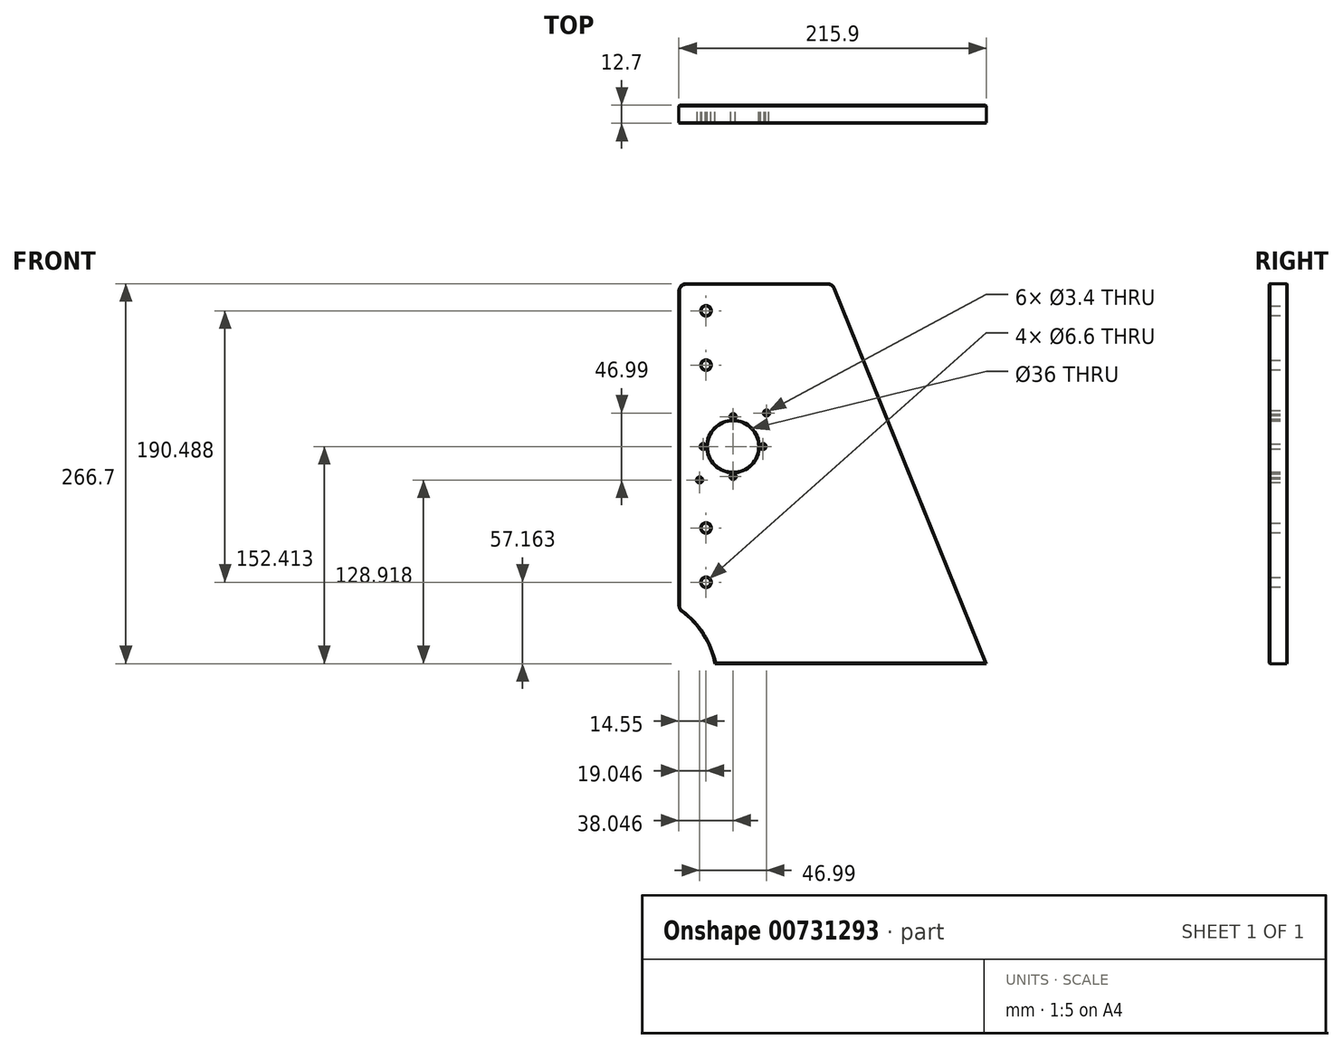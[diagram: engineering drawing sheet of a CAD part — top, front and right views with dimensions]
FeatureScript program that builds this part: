
annotation { "Feature Type Name" : "Feature", "Feature Type Description" : "" }
export const myFeature = defineFeature(function(context is Context, id is Id, definition is map)
    precondition{}
    {
        {
            var Q0;
            Q0=qCreatedBy(makeId("Front.planeOp"),FACE);
            var sketch = newSketch(context, id + "F0", { "sketchPlane" : qUnion([Q0])});
            skLineSegment(sketch, "E0.bottom", {"start": v(108.43, 152.4) * mm, "end": v(-107.47, 152.4) * mm});
            skLineSegment(sketch, "E0.left", {"start": v(108.43, 152.4) * mm, "end": v(108.43, -114.3) * mm});
            skLineSegment(sketch, "E0.right", {"start": v(-107.47, 152.4) * mm, "end": v(-107.47, -114.3) * mm});
            skPoint(sketch, "E0.middle", {"position": v(0, 0) * mm});
            skCircle(sketch, "E1", {"center": v(-88.42, -57.14) * mm, "radius": 3.3 * mm});
            skCircle(sketch, "E2", {"center": v(-88.42, -19.04) * mm, "radius": 3.3 * mm});
            skCircle(sketch, "E3", {"center": v(-88.42, 95.25) * mm, "radius": 3.3 * mm});
            skCircle(sketch, "E4", {"center": v(-88.42, 133.35) * mm, "radius": 3.3 * mm});
            skLineSegment(sketch, "E5", {"start": v(-107.47, -114.3) * mm, "end": v(108.43, -114.3) * mm});
            skLineSegment(sketch, "E6", {"start": v(-107.47, -76.2) * mm, "end": v(108.43, -76.2) * mm, "construction": true});
            skPoint(sketch, "E7.middle", {"position": v(-69.42, 38.11) * mm});
            skLineSegment(sketch, "E8", {"start": v(-69.42, 74.31) * mm, "end": v(-69.42, 11.11) * mm, "construction": true});
            skPoint(sketch, "E9.startSnap0", {"position": v(0.48, 152.4) * mm});
            skCircle(sketch, "E10", {"center": v(-69.42, 38.11) * mm, "radius": 18 * mm});
            skLineSegment(sketch, "E11", {"start": v(-98.77, 38.11) * mm, "end": v(-40.23, 38.11) * mm, "construction": true});
            skLineSegment(sketch, "E12", {"start": v(-91.1, 59.79) * mm, "end": v(-42.84, 11.53) * mm, "construction": true});
            skLineSegment(sketch, "E13", {"start": v(-49.22, 58.32) * mm, "end": v(-94.15, 13.39) * mm, "construction": true});
            skCircle(sketch, "E14", {"center": v(-92.92, 61.6) * mm, "radius": 1.7 * mm});
            skCircle(sketch, "E15.MirrorC", {"center": v(-92.92, 14.62) * mm, "radius": 1.7 * mm});
            skCircle(sketch, "E16.MirrorC", {"center": v(-45.93, 61.6) * mm, "radius": 1.7 * mm});
            skCircle(sketch, "E17.MirrorC", {"center": v(-45.93, 14.62) * mm, "radius": 1.7 * mm});
            skCircle(sketch, "E18", {"center": v(-69.42, 59.11) * mm, "radius": 1.7 * mm});
            skCircle(sketch, "E19.MirrorC", {"center": v(-69.42, 17.11) * mm, "radius": 1.7 * mm});
            skCircle(sketch, "E20", {"center": v(-90.42, 38.11) * mm, "radius": 1.7 * mm});
            skCircle(sketch, "E21.MirrorC", {"center": v(-48.42, 38.11) * mm, "radius": 1.7 * mm});
            skLineSegment(sketch, "E22", {"start": v(0.48, 152.4) * mm, "end": v(108.43, -114.3) * mm});
            skArc(sketch, "E23", {"start": v(-82.07, -114.3) * mm, "mid": v(-91, -92.73) * mm, "end": v(-107.47, -76.2) * mm});
            skSolve(sketch);
        }
        {
            var Q0;
            Q0=makeQuery(id+"F0.imprint","IMPRINT",FACE,{"disambiguationData":[TD([[makeQuery(id+"F0.imprint","IMPRINT",EDGE,{"derivedFrom":sQuery(id+"F0.wireOp",EDGE,"E1")}),-1.0]])]});
            var Q1;
            Q1=makeQuery(id+"F0.imprint","IMPRINT",FACE,{"disambiguationData":[TD([[makeQuery(id+"F0.imprint","IMPRINT",EDGE,{"derivedFrom":sQuery(id+"F0.wireOp",EDGE,"E15.MirrorC")}),-1.0]])]});
            var Q2;
            Q2=makeQuery(id+"F0.imprint","IMPRINT",FACE,{"disambiguationData":[TD([[makeQuery(id+"F0.imprint","IMPRINT",EDGE,{"derivedFrom":sQuery(id+"F0.wireOp",EDGE,"E17.MirrorC")}),1.0]])]});
            var Q3;
            Q3=makeQuery(id+"F0.imprint","IMPRINT",FACE,{"disambiguationData":[TD([[makeQuery(id+"F0.imprint","IMPRINT",EDGE,{"derivedFrom":sQuery(id+"F0.wireOp",EDGE,"E16.MirrorC")}),-1.0]])]});
            var Q4;
            Q4=makeQuery(id+"F0.imprint","IMPRINT",FACE,{"disambiguationData":[TD([[makeQuery(id+"F0.imprint","IMPRINT",EDGE,{"derivedFrom":sQuery(id+"F0.wireOp",EDGE,"E14")}),1.0]])]});
            extrude(context, id + "F1", {"entities" : qUnion([Q0, Q1, Q2, Q3, Q4]), "depth" : 12.7 * mm, "offsetDistance" : 25.4 * mm});
        }
        {
            var Q0;
            Q0=makeQuery(id+"F1.opExtrude","SWEPT_EDGE",EDGE,{"disambiguationData":[OSD([sQuery(id+"F0.wireOp",EDGE,"E0.bottom"),sQuery(id+"F0.wireOp",EDGE,"E0.right")])]});
            var Q1;
            Q1=makeQuery(id+"F1.opExtrude","SWEPT_EDGE",EDGE,{"disambiguationData":[OSD([sQuery(id+"F0.wireOp",EDGE,"E0.bottom"),sQuery(id+"F0.wireOp",EDGE,"E22")])]});
            var Q2;
            Q2=makeQuery(id+"F1.opExtrude","SWEPT_EDGE",EDGE,{"disambiguationData":[OSD([sQuery(id+"F0.wireOp",EDGE,"E0.right"),sQuery(id+"F0.wireOp",EDGE,"E23")])]});
            fillet(context, id + "F2", {"entities" : qUnion([Q0, Q1, Q2]), "radius" : 5.08 * mm, "tangentPropagation" : true, "allowEdgeOverflow" : false});
        }
        {
            var Q0;
            Q0=makeQuery(id+"F1.opExtrude","CAP_FACE",FACE,{"disambiguationData":[OSD([sQuery(id+"F0.wireOp",EDGE,"E0.bottom"),sQuery(id+"F0.wireOp",EDGE,"E0.right"),sQuery(id+"F0.wireOp",EDGE,"E1"),sQuery(id+"F0.wireOp",EDGE,"E2"),sQuery(id+"F0.wireOp",EDGE,"E3"),sQuery(id+"F0.wireOp",EDGE,"E4"),sQuery(id+"F0.wireOp",EDGE,"E5"),sQuery(id+"F0.wireOp",EDGE,"E10"),sQuery(id+"F0.wireOp",EDGE,"E14"),sQuery(id+"F0.wireOp",EDGE,"E15.MirrorC"),sQuery(id+"F0.wireOp",EDGE,"E16.MirrorC"),sQuery(id+"F0.wireOp",EDGE,"E17.MirrorC"),sQuery(id+"F0.wireOp",EDGE,"E18"),sQuery(id+"F0.wireOp",EDGE,"E19.MirrorC"),sQuery(id+"F0.wireOp",EDGE,"E20"),sQuery(id+"F0.wireOp",EDGE,"E21.MirrorC"),sQuery(id+"F0.wireOp",EDGE,"E22"),sQuery(id+"F0.wireOp",EDGE,"E23")])],"isStart":false});
            var Q1;
            Q1=makeQuery(id+"F1.opExtrude","CAP_FACE",FACE,{"disambiguationData":[OSD([sQuery(id+"F0.wireOp",EDGE,"E0.bottom"),sQuery(id+"F0.wireOp",EDGE,"E0.right"),sQuery(id+"F0.wireOp",EDGE,"E1"),sQuery(id+"F0.wireOp",EDGE,"E2"),sQuery(id+"F0.wireOp",EDGE,"E3"),sQuery(id+"F0.wireOp",EDGE,"E4"),sQuery(id+"F0.wireOp",EDGE,"E5"),sQuery(id+"F0.wireOp",EDGE,"E10"),sQuery(id+"F0.wireOp",EDGE,"E14"),sQuery(id+"F0.wireOp",EDGE,"E15.MirrorC"),sQuery(id+"F0.wireOp",EDGE,"E16.MirrorC"),sQuery(id+"F0.wireOp",EDGE,"E17.MirrorC"),sQuery(id+"F0.wireOp",EDGE,"E18"),sQuery(id+"F0.wireOp",EDGE,"E19.MirrorC"),sQuery(id+"F0.wireOp",EDGE,"E20"),sQuery(id+"F0.wireOp",EDGE,"E21.MirrorC"),sQuery(id+"F0.wireOp",EDGE,"E22"),sQuery(id+"F0.wireOp",EDGE,"E23")])],"isStart":true});
            chamfer(context, id + "F3", {"entities" : qUnion([Q0, Q1]), "width" : 0.5 * mm});
        }
    });
